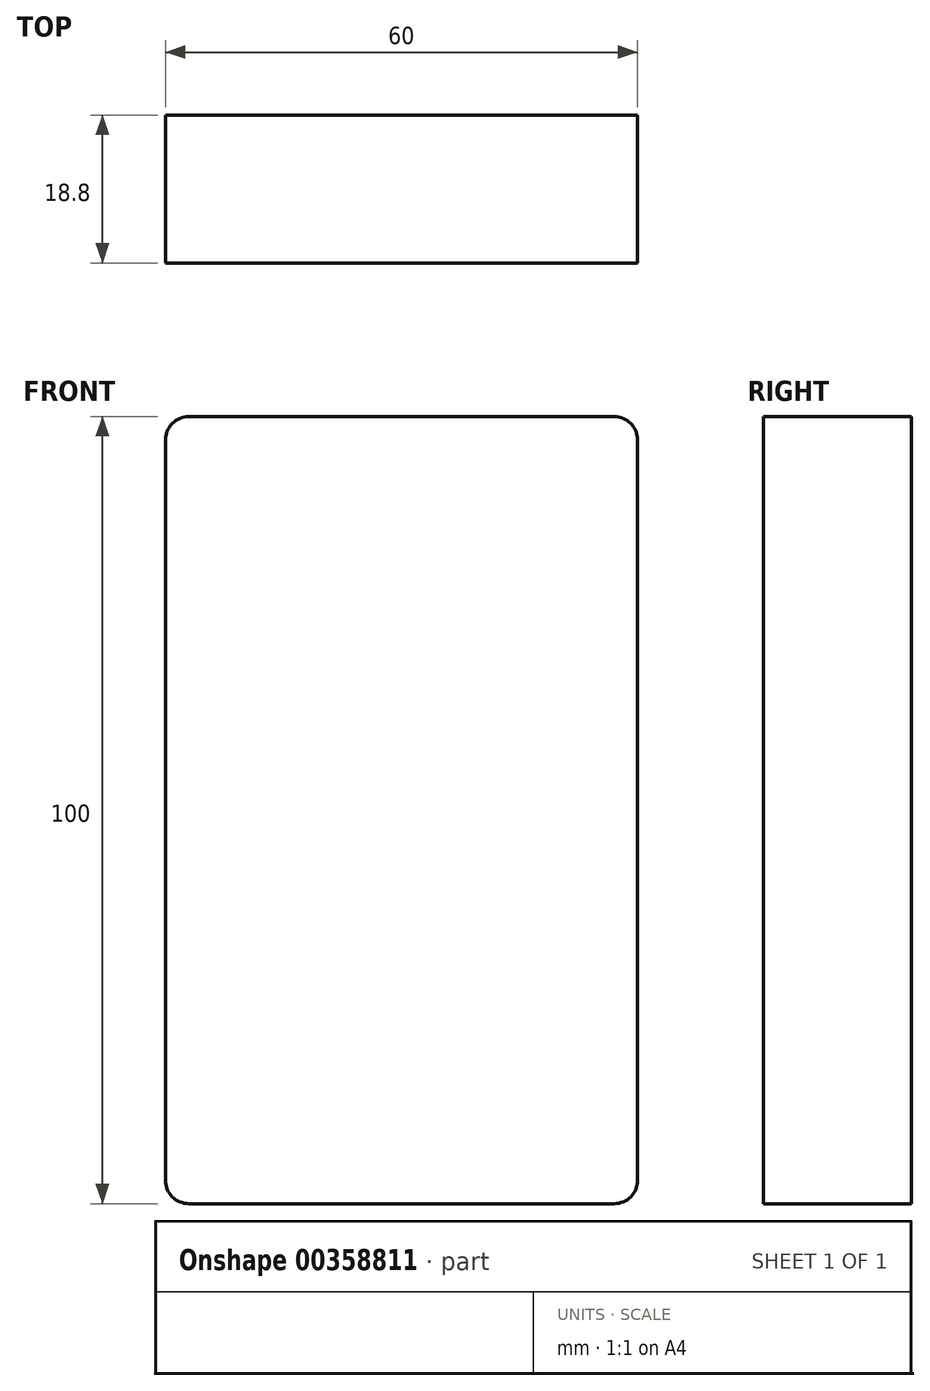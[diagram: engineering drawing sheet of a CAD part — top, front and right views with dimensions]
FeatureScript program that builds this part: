
annotation { "Feature Type Name" : "Feature", "Feature Type Description" : "" }
export const myFeature = defineFeature(function(context is Context, id is Id, definition is map)
    precondition{}
    {
        {
            var Q0;
            Q0=qCreatedBy(makeId("Front.planeOp"),FACE);
            var sketch = newSketch(context, id + "F0", { "sketchPlane" : qUnion([Q0])});
            skLineSegment(sketch, "E0", {"start": v(-78.95, -67.88) * mm, "end": v(-24.95, -67.88) * mm});
            skLineSegment(sketch, "E1", {"start": v(-21.95, -64.88) * mm, "end": v(-21.95, 29.12) * mm});
            skLineSegment(sketch, "E2", {"start": v(-24.95, 32.12) * mm, "end": v(-78.95, 32.12) * mm});
            skLineSegment(sketch, "E3", {"start": v(-81.95, 29.12) * mm, "end": v(-81.95, -64.88) * mm});
            skPoint(sketch, "E4.start.orphan", {"position": v(-21.95, 30.52) * mm});
            skPoint(sketch, "E5.start.orphan", {"position": v(-81.95, 30.52) * mm});
            skLineSegment(sketch, "E6", {"start": v(-25.55, -61.28) * mm, "end": v(-25.55, 25.52) * mm});
            skLineSegment(sketch, "E7", {"start": v(-28.55, -64.28) * mm, "end": v(-75.35, -64.28) * mm});
            skLineSegment(sketch, "E8", {"start": v(-78.35, -61.28) * mm, "end": v(-78.35, 25.52) * mm});
            skPoint(sketch, "E9.end.orphan", {"position": v(-71.05, 30.52) * mm});
            skLineSegment(sketch, "E10", {"start": v(-28.55, 28.52) * mm, "end": v(-75.35, 28.52) * mm});
            skPoint(sketch, "E11.start.orphan", {"position": v(-25.55, -67.88) * mm});
            skPoint(sketch, "E12.visualSharp", {"position": v(-81.95, 32.12) * mm});
            skArc(sketch, "E12.filletArc", {"start": v(-78.95, 32.12) * mm, "mid": v(-81.07, 31.24) * mm, "end": v(-81.95, 29.12) * mm});
            skPoint(sketch, "E13.visualSharp", {"position": v(-21.95, 32.12) * mm});
            skArc(sketch, "E13.filletArc", {"start": v(-21.95, 29.12) * mm, "mid": v(-22.83, 31.24) * mm, "end": v(-24.95, 32.12) * mm});
            skPoint(sketch, "E14.visualSharp", {"position": v(-21.95, -67.88) * mm});
            skArc(sketch, "E14.filletArc", {"start": v(-24.95, -67.88) * mm, "mid": v(-22.83, -67) * mm, "end": v(-21.95, -64.88) * mm});
            skPoint(sketch, "E15.visualSharp", {"position": v(-81.95, -67.88) * mm});
            skArc(sketch, "E15.filletArc", {"start": v(-81.95, -64.88) * mm, "mid": v(-81.07, -67) * mm, "end": v(-78.95, -67.88) * mm});
            skPoint(sketch, "E16.visualSharp", {"position": v(-78.35, -64.28) * mm});
            skArc(sketch, "E16.filletArc", {"start": v(-78.35, -61.28) * mm, "mid": v(-77.47, -63.4) * mm, "end": v(-75.35, -64.28) * mm});
            skPoint(sketch, "E17.visualSharp", {"position": v(-25.55, -64.28) * mm});
            skArc(sketch, "E17.filletArc", {"start": v(-28.55, -64.28) * mm, "mid": v(-26.43, -63.4) * mm, "end": v(-25.55, -61.28) * mm});
            skPoint(sketch, "E18.visualSharp", {"position": v(-25.55, 28.52) * mm});
            skArc(sketch, "E18.filletArc", {"start": v(-25.55, 25.52) * mm, "mid": v(-26.43, 27.64) * mm, "end": v(-28.55, 28.52) * mm});
            skPoint(sketch, "E19.visualSharp", {"position": v(-78.35, 28.52) * mm});
            skArc(sketch, "E19.filletArc", {"start": v(-75.35, 28.52) * mm, "mid": v(-77.47, 27.64) * mm, "end": v(-78.35, 25.52) * mm});
            skSolve(sketch);
        }
        {
            var Q0;
            Q0=makeQuery(id+"F0.imprint","IMPRINT",FACE,{"disambiguationData":[TD([[makeQuery(id+"F0.imprint","IMPRINT",EDGE,{"derivedFrom":sQuery(id+"F0.wireOp",EDGE,"E6")}),1.0]])]});
            var Q1;
            Q1=makeQuery(id+"F0.imprint","IMPRINT",FACE,{"disambiguationData":[TD([[makeQuery(id+"F0.imprint","IMPRINT",EDGE,{"derivedFrom":sQuery(id+"F0.wireOp",EDGE,"E0")}),1.0]])]});
            extrude(context, id + "F1", {"entities" : qUnion([Q0, Q1]), "depth" : 18.8 * mm});
        }
    });
